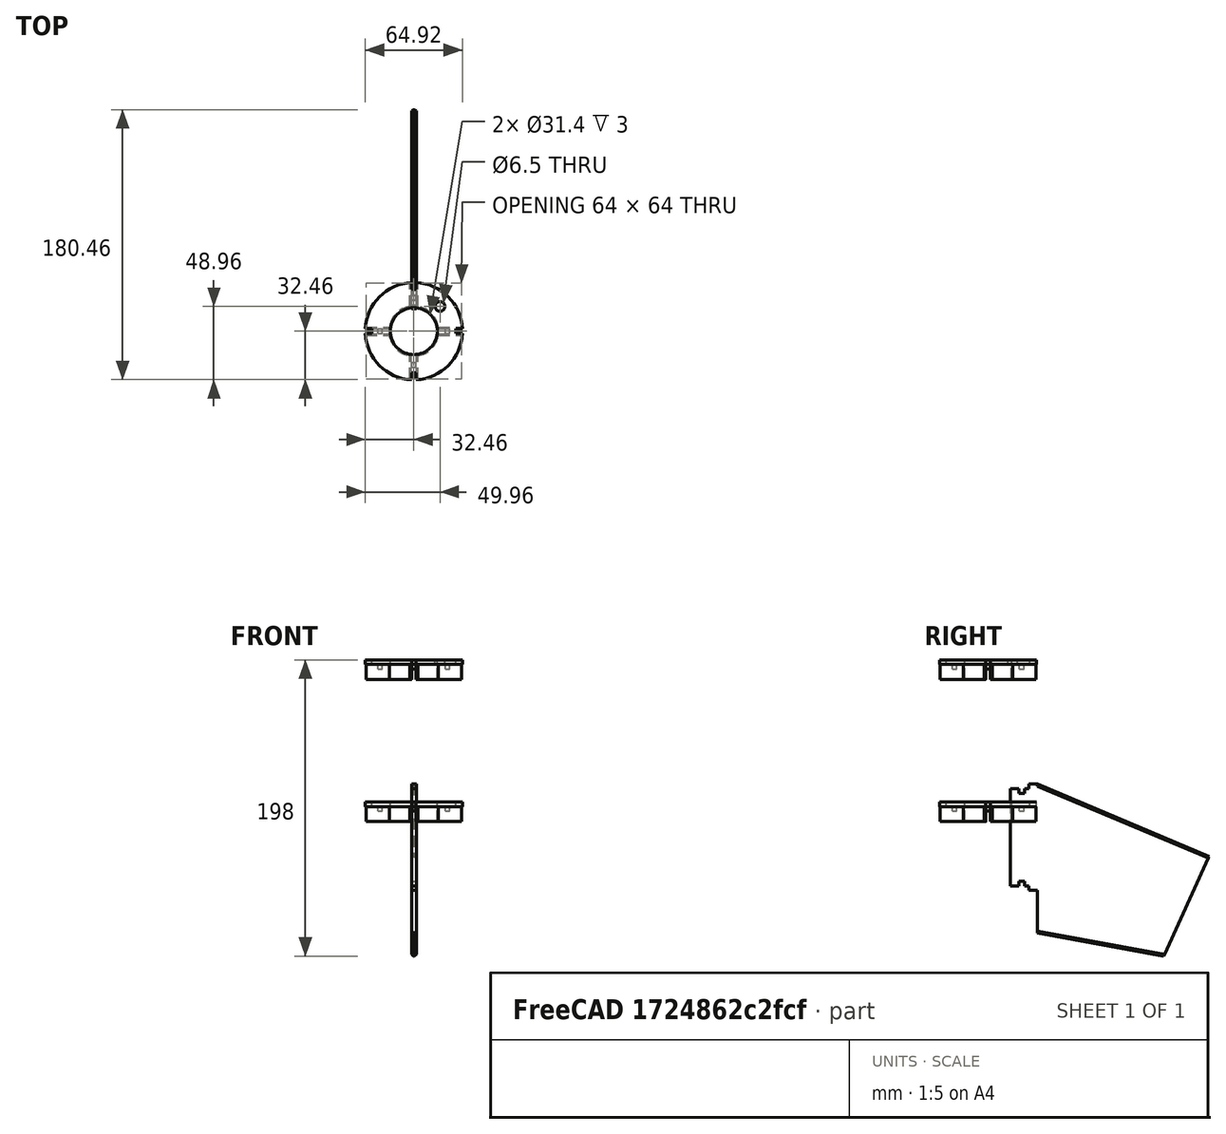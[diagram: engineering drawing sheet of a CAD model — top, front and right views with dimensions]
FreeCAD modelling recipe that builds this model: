
FCSTD DOCUMENT  (FreeCAD 0.19R24366 (Git))
Label: HobgoblinParts
License: All rights reserved
LicenseURL: http://en.wikipedia.org/wiki/All_rights_reserved
objects: Part::Box×47, Part::MultiFuse×13, Part::FeaturePython×10, Part::Cut×4, Part::Feature×2, Part::Cylinder×1, Part::Part2DObjectPython×1, Part::Extrusion×1, Part::Chamfer×1
note: 80 computed .brp shape members not serialized (recipe doc carries the construction recipe); baked Part::Feature solids carry a one-line shape summary decoded from their .brp

FEATURE [Part::FeaturePython] Tube  # WARN: FeaturePython — macro-defined, semantics opaque (R4)
  AttacherType = Attacher::AttachEngine3D
  Height = 3
  InnerRadius = 15.7
  OuterRadius = 32.5
FEATURE [Part::Box] Box  label="FinCut001"
  AttacherType = Attacher::AttachEngine3D
  Height = 3
  Length = 3.1
  Placement = pos=(-1.55,-34,0) rot=(0,0,1;0rad)
  Width = 6
  expr: .Placement.Base.x = -3.1 / 2
FEATURE [Part::Box] Box001  label="FinCut002"
  AttacherType = Attacher::AttachEngine3D
  Height = 3
  Length = 3.1
  Placement = pos=(-1.55,28,0) rot=(0,0,1;0rad)
  Width = 6
  expr: .Placement.Base.x = -3.1 / 2
FEATURE [Part::Box] Box002  label="FinCut003"
  AttacherType = Attacher::AttachEngine3D
  Height = 3
  Length = 6
  Placement = pos=(28,-1.55,0) rot=(0,0,1;0rad)
  Width = 3.1
FEATURE [Part::Box] Box003  label="FinCut004"
  AttacherType = Attacher::AttachEngine3D
  Height = 3
  Length = 6
  Placement = pos=(-34,-1.55,0) rot=(0,0,1;0rad)
  Width = 3.1
FEATURE [Part::MultiFuse] Fusion  label="OuterFinCutouts"
  Shapes = -> [Box,Box001,Box002,Box003]
FEATURE [Part::FeaturePython] Tube001  label="InnerTube"  # WARN: FeaturePython — macro-defined, semantics opaque (R4)
  AttacherType = Attacher::AttachEngine3D
  Height = 10
  InnerRadius = 15.7
  OuterRadius = 16.7
  Placement = pos=(0,0,-10) rot=(0,0,1;0rad)
FEATURE [Part::Box] Box004  label="Alignment001"
  AttacherType = Attacher::AttachEngine3D
  Height = 10
  Length = 1
  Placement = pos=(1.7,16,-10) rot=(0,0,1;0rad)
  Width = 16
FEATURE [Part::Box] Box005  label="Alignment002"
  AttacherType = Attacher::AttachEngine3D
  Height = 10
  Length = 1
  Placement = pos=(-2.7,16,-10) rot=(0,0,1;0rad)
  Width = 16
FEATURE [Part::Box] Box006  label="Alignment003"
  AttacherType = Attacher::AttachEngine3D
  Height = 10
  Length = 1
  Placement = pos=(-2.7,-32,-10) rot=(0,0,1;0rad)
  Width = 16
FEATURE [Part::Box] Box007  label="Alignment004"
  AttacherType = Attacher::AttachEngine3D
  Height = 10
  Length = 1
  Placement = pos=(1.7,-32,-10) rot=(0,0,1;0rad)
  Width = 16
FEATURE [Part::Box] Box008  label="Alignment005"
  AttacherType = Attacher::AttachEngine3D
  Height = 10
  Length = 16
  Placement = pos=(16,1.7,-10) rot=(0,0,1;0rad)
  Width = 1
FEATURE [Part::Box] Box009  label="Alignment006"
  AttacherType = Attacher::AttachEngine3D
  Height = 10
  Length = 16
  Placement = pos=(16,-2.7,-10) rot=(0,0,1;0rad)
  Width = 1
FEATURE [Part::Box] Box010  label="Alignment007"
  AttacherType = Attacher::AttachEngine3D
  Height = 10
  Length = 16
  Placement = pos=(-32,1.7,-10) rot=(0,0,1;0rad)
  Width = 1
FEATURE [Part::Box] Box011  label="Alignment008"
  AttacherType = Attacher::AttachEngine3D
  Height = 10
  Length = 16
  Placement = pos=(-32,-2.7,-10) rot=(0,0,1;0rad)
  Width = 1
FEATURE [Part::MultiFuse] Fusion001  label="AlignmentTabs"
  Shapes = -> [Box004,Box005,Box006,Box007,Box008,Box009,Box010,Box011]
FEATURE [Part::Cylinder] Cylinder  label="EyeboltCutout"
  Angle = 360
  AttacherType = Attacher::AttachEngine3D
  Height = 10
  Placement = pos=(17.5,16.5,91) rot=(0,0,1;0rad)
  Radius = 3.25
  expr: Radius = 6.5 / 2
FEATURE [Part::Box] Box012  label="FinCut005"
  AttacherType = Attacher::AttachEngine3D
  Height = 10
  Length = 3.1
  Placement = pos=(-1.55,-21,-10) rot=(0,0,1;0rad)
  Width = 6
  expr: .Placement.Base.x = -3.1 / 2
FEATURE [Part::Box] Box013  label="FinCut006"
  AttacherType = Attacher::AttachEngine3D
  Height = 10
  Length = 3.1
  Placement = pos=(-1.55,15,-10) rot=(0,0,1;0rad)
  Width = 6
  expr: .Placement.Base.x = -3.1 / 2
FEATURE [Part::Box] Box014  label="FinCut007"
  AttacherType = Attacher::AttachEngine3D
  Height = 10
  Length = 6
  Placement = pos=(15,-1.55,-10) rot=(0,0,1;0rad)
  Width = 3.1
FEATURE [Part::Box] Box015  label="FinCut008"
  AttacherType = Attacher::AttachEngine3D
  Height = 10
  Length = 6
  Placement = pos=(-21,-1.55,-10) rot=(0,0,1;0rad)
  Width = 3.1
FEATURE [Part::MultiFuse] Fusion002  label="InnerFinCutouts"
  Shapes = -> [Box015,Box012,Box013,Box014]
FEATURE [Part::MultiFuse] Fusion003  label="FinCutouts"
  Shapes = -> [Fusion,Fusion002]
FEATURE [Part::MultiFuse] Fusion004  label="RingPlusAlignmentTabs"
  Shapes = -> [Tube,Tube001,Fusion001]
FEATURE [Part::Cut] Cut  label="CenteringRingWithAlignmentTabs"
  Base = -> Fusion004
  Tool = -> Fusion003
FEATURE [Part::Box] Box016  label="FinLock001"
  AttacherType = Attacher::AttachEngine3D
  Height = 3
  Length = 3
  Placement = pos=(21,-1.5,-3) rot=(0,0,1;0rad)
  Width = 3
FEATURE [Part::Box] Box017  label="FinLock002"
  AttacherType = Attacher::AttachEngine3D
  Height = 3
  Length = 3
  Placement = pos=(-1.5,21,-3) rot=(0,0,1;0rad)
  Width = 3
FEATURE [Part::Box] Box018  label="FinLock003"
  AttacherType = Attacher::AttachEngine3D
  Height = 3
  Length = 3
  Placement = pos=(-1.5,-24,-3) rot=(0,0,1;0rad)
  Width = 3
FEATURE [Part::Box] Box019  label="FinLock004"
  AttacherType = Attacher::AttachEngine3D
  Height = 3
  Length = 3
  Placement = pos=(-24,-1.5,-3) rot=(0,0,1;0rad)
  Width = 3
FEATURE [Part::MultiFuse] Fusion005  label="FinLocks"
  Shapes = -> [Box016,Box017,Box018,Box019]
FEATURE [Part::FeaturePython] Connect  label="CenteringRingWithAlignmentAndFinlocks"  # WARN: FeaturePython — macro-defined, semantics opaque (R4)
  Objects = -> [Cut,Fusion005]
  Tolerance = 0
FEATURE [Part::Box] Box028  label="FinLock013"
  AttacherType = Attacher::AttachEngine3D
  Height = 3
  Length = 3
  Placement = pos=(21,-1.5,-3) rot=(0,0,1;0rad)
  Width = 3
FEATURE [Part::Box] Box029  label="FinLock014"
  AttacherType = Attacher::AttachEngine3D
  Height = 3
  Length = 3
  Placement = pos=(-24,-1.5,-3) rot=(0,0,1;0rad)
  Width = 3
FEATURE [Part::Box] Box030  label="FinLock015"
  AttacherType = Attacher::AttachEngine3D
  Height = 3
  Length = 3
  Placement = pos=(-1.5,21,-3) rot=(0,0,1;0rad)
  Width = 3
FEATURE [Part::FeaturePython] Tube002  # WARN: FeaturePython — macro-defined, semantics opaque (R4)
  AttacherType = Attacher::AttachEngine3D
  Height = 3
  InnerRadius = 15.7
  OuterRadius = 32.5
FEATURE [Part::Box] Box031  label="FinCut009"
  AttacherType = Attacher::AttachEngine3D
  Height = 3
  Length = 3.1
  Placement = pos=(-1.55,-34,0) rot=(0,0,1;0rad)
  Width = 6
  expr: .Placement.Base.x = -3.1 / 2
FEATURE [Part::Box] Box032  label="FinCut010"
  AttacherType = Attacher::AttachEngine3D
  Height = 3
  Length = 3.1
  Placement = pos=(-1.55,28,0) rot=(0,0,1;0rad)
  Width = 6
  expr: .Placement.Base.x = -3.1 / 2
FEATURE [Part::Box] Box033  label="FinCut011"
  AttacherType = Attacher::AttachEngine3D
  Height = 3
  Length = 6
  Placement = pos=(28,-1.55,0) rot=(0,0,1;0rad)
  Width = 3.1
FEATURE [Part::Box] Box034  label="FinCut012"
  AttacherType = Attacher::AttachEngine3D
  Height = 3
  Length = 6
  Placement = pos=(-34,-1.55,0) rot=(0,0,1;0rad)
  Width = 3.1
FEATURE [Part::MultiFuse] Fusion009  label="OuterFinCutouts001"
  Shapes = -> [Box031,Box032,Box033,Box034]
FEATURE [Part::FeaturePython] Tube003  label="InnerTube001"  # WARN: FeaturePython — macro-defined, semantics opaque (R4)
  AttacherType = Attacher::AttachEngine3D
  Height = 10
  InnerRadius = 15.7
  OuterRadius = 16.7
  Placement = pos=(0,0,-10) rot=(0,0,1;0rad)
FEATURE [Part::Box] Box035  label="Alignment009"
  AttacherType = Attacher::AttachEngine3D
  Height = 10
  Length = 1
  Placement = pos=(1.7,16,-10) rot=(0,0,1;0rad)
  Width = 16
FEATURE [Part::Box] Box036  label="Alignment010"
  AttacherType = Attacher::AttachEngine3D
  Height = 10
  Length = 1
  Placement = pos=(-2.7,16,-10) rot=(0,0,1;0rad)
  Width = 16
FEATURE [Part::Box] Box037  label="Alignment011"
  AttacherType = Attacher::AttachEngine3D
  Height = 10
  Length = 1
  Placement = pos=(-2.7,-32,-10) rot=(0,0,1;0rad)
  Width = 16
FEATURE [Part::Box] Box038  label="Alignment012"
  AttacherType = Attacher::AttachEngine3D
  Height = 10
  Length = 1
  Placement = pos=(1.7,-32,-10) rot=(0,0,1;0rad)
  Width = 16
FEATURE [Part::Box] Box039  label="Alignment013"
  AttacherType = Attacher::AttachEngine3D
  Height = 10
  Length = 16
  Placement = pos=(16,1.7,-10) rot=(0,0,1;0rad)
  Width = 1
FEATURE [Part::Box] Box040  label="Alignment014"
  AttacherType = Attacher::AttachEngine3D
  Height = 10
  Length = 16
  Placement = pos=(16,-2.7,-10) rot=(0,0,1;0rad)
  Width = 1
FEATURE [Part::Box] Box041  label="Alignment015"
  AttacherType = Attacher::AttachEngine3D
  Height = 10
  Length = 16
  Placement = pos=(-32,1.7,-10) rot=(0,0,1;0rad)
  Width = 1
FEATURE [Part::Box] Box042  label="Alignment016"
  AttacherType = Attacher::AttachEngine3D
  Height = 10
  Length = 16
  Placement = pos=(-32,-2.7,-10) rot=(0,0,1;0rad)
  Width = 1
FEATURE [Part::MultiFuse] Fusion010  label="AlignmentTabs001"
  Shapes = -> [Box035,Box036,Box037,Box038,Box039,Box040,Box041,Box042]
FEATURE [Part::Box] Box043  label="FinCut013"
  AttacherType = Attacher::AttachEngine3D
  Height = 10
  Length = 3.1
  Placement = pos=(-1.55,-21,-10) rot=(0,0,1;0rad)
  Width = 6
  expr: .Placement.Base.x = -3.1 / 2
FEATURE [Part::Box] Box044  label="FinCut014"
  AttacherType = Attacher::AttachEngine3D
  Height = 10
  Length = 3.1
  Placement = pos=(-1.55,15,-10) rot=(0,0,1;0rad)
  Width = 6
  expr: .Placement.Base.x = -3.1 / 2
FEATURE [Part::Box] Box045  label="FinCut015"
  AttacherType = Attacher::AttachEngine3D
  Height = 10
  Length = 6
  Placement = pos=(15,-1.55,-10) rot=(0,0,1;0rad)
  Width = 3.1
FEATURE [Part::Box] Box046  label="FinCut016"
  AttacherType = Attacher::AttachEngine3D
  Height = 10
  Length = 6
  Placement = pos=(-21,-1.55,-10) rot=(0,0,1;0rad)
  Width = 3.1
FEATURE [Part::MultiFuse] Fusion011  label="InnerFinCutouts001"
  Shapes = -> [Box046,Box043,Box044,Box045]
FEATURE [Part::MultiFuse] Fusion012  label="FinCutouts001"
  Shapes = -> [Fusion009,Fusion011]
FEATURE [Part::MultiFuse] Fusion013  label="RingPlusAlignmentTabs001"
  Shapes = -> [Tube002,Tube003,Fusion010]
FEATURE [Part::Cut] Cut003  label="CenteringRingWithAlignmentTabs001"
  Base = -> Fusion013
  Tool = -> Fusion012
FEATURE [Part::Box] Box047  label="FinLock016"
  AttacherType = Attacher::AttachEngine3D
  Height = 3
  Length = 3
  Placement = pos=(-1.5,-24,-3) rot=(0,0,1;0rad)
  Width = 3
FEATURE [Part::MultiFuse] Fusion014  label="FinLocks001"
  Shapes = -> [Box028,Box030,Box047,Box029]
FEATURE [Part::FeaturePython] Connect001  label="CenteringRingWithAlignmentAndFinlocks001"  # WARN: FeaturePython — macro-defined, semantics opaque (R4)
  Objects = -> [Cut003,Fusion014]
  Placement = pos=(0,0,95) rot=(0,0,1;0rad)
  Tolerance = 0
FEATURE [Part::Cut] Cut004  label="CenteringRingWIthAlignmentAndFinlocksAndEyeboltCutout"
  Base = -> Connect001
  Tool = -> Cylinder
FEATURE [Part::Feature] Connect_solid  label="CenteringRingWithAlignmentAndFinlocks (Solid)"
  shape: bbox 64.93 x 64.93 x 13 mm, 115 faces (baked)
FEATURE [Part::Part2DObjectPython] Wire  # Draft 2D object (typed FeaturePython)
  Area = 8782.49
  ChamferSize = 0
  Closed = true
  End = (99.6,0,0)
  FilletRadius = 0
  Length = 383.623
  MakeFace = true
  Placement = pos=(0,0,0) rot=(0,-1,0;0.785397rad)
  Points = (4) [(0,0,0),(34.1533,115,-34.1532),(81.3174,84.6,-81.3172),(70.4279,0,-70.4278)]
  Start = (0,0,0)
  Subdivisions = 0
FEATURE [Part::Box] Box051  label="AlignmentTab001"
  AttacherType = Attacher::AttachEngine3D
  Height = 3
  Length = 3
  Placement = pos=(0,-6,0) rot=(0,0,1;0rad)
  Width = 6
FEATURE [Part::Box] Box052  label="AlignmentTab002"
  AttacherType = Attacher::AttachEngine3D
  Height = 3
  Length = 3
  Placement = pos=(68,-6,0) rot=(0,0,1;0rad)
  Width = 6
FEATURE [Part::Extrusion] Extrude
  Base = -> Wire
  Dir = (0,0,1)
  DirMode = 0
  FaceMakerClass = Part::FaceMakerBullseye
  LengthFwd = 3
  LengthRev = 0
  Solid = false
  Symmetric = false
FEATURE [Part::Chamfer] Chamfer  label="Fin"
  Base = -> Extrude
  Edges = 4 edges r=1.3: [Edge3,Edge4,Edge9,Edge10]
FEATURE [Part::Box] Box053  label="FinTabMain"
  AttacherType = Attacher::AttachEngine3D
  Height = 3
  Length = 65
  Placement = pos=(3,-18,0) rot=(0,0,1;0rad)
  Width = 18
FEATURE [Part::FeaturePython] Connect003  # WARN: FeaturePython — macro-defined, semantics opaque (R4)
  Objects = -> [Box053,Box051,Box052]
  Tolerance = 0
FEATURE [Part::FeaturePython] Connect002  label="GoblinUpscaleFin"  # WARN: FeaturePython — macro-defined, semantics opaque (R4)
  Objects = -> [Connect003,Chamfer]
  Placement = pos=(-1.4,33,15) rot=(0,1,0;1.5708rad)
  Tolerance = 0
FEATURE [Part::Box] Box054  label="AftFinLockCutout001"
  AttacherType = Attacher::AttachEngine3D
  Height = 3
  Length = 3
  Placement = pos=(-1.5,20.7,-73) rot=(0,0,1;0rad)
  Width = 3.6
FEATURE [Part::Box] Box055  label="ForwardFinLockCutout001"
  AttacherType = Attacher::AttachEngine3D
  Height = 3
  Length = 3
  Placement = pos=(-1.5,20.7,-3) rot=(0,0,1;0rad)
  Width = 3.6
FEATURE [Part::Box] Box056  label="TabTrim003"
  AttacherType = Attacher::AttachEngine3D
  Height = 10
  Length = 10
  Placement = pos=(-4.3,17.4,0) rot=(0,0,1;0rad)
  Width = 10
FEATURE [Part::Box] Box057  label="TabTrim004"
  AttacherType = Attacher::AttachEngine3D
  Height = 10
  Length = 10
  Placement = pos=(-4.3,17.4,-83) rot=(0,0,1;0rad)
  Width = 10
FEATURE [Part::FeaturePython] Connect004  # WARN: FeaturePython — macro-defined, semantics opaque (R4)
  Objects = -> [Box055,Box056]
  Placement = pos=(0,0,11.9) rot=(0,0,1;0rad)
  Tolerance = 0
FEATURE [Part::FeaturePython] Connect005  # WARN: FeaturePython — macro-defined, semantics opaque (R4)
  Objects = -> [Box054,Box057]
  Placement = pos=(0,0,20) rot=(0,0,1;0rad)
  Tolerance = 0
FEATURE [Part::MultiFuse] Fusion015  label="Alignment Cutouts"
  Placement = pos=(0.1,0,0) rot=(0,0,1;0rad)
  Shapes = -> [Connect004,Connect005]
FEATURE [Part::Cut] Cut005  label="GoblinUpscaleFinForwardTab"
  Base = -> Connect002
  Tool = -> Fusion015
FEATURE [Part::Feature] Cut005_solid  label="GoblinUpscaleFinForwardTab (Solid)"
  shape: bbox 3 x 133 x 115 mm, 37 faces (baked)
